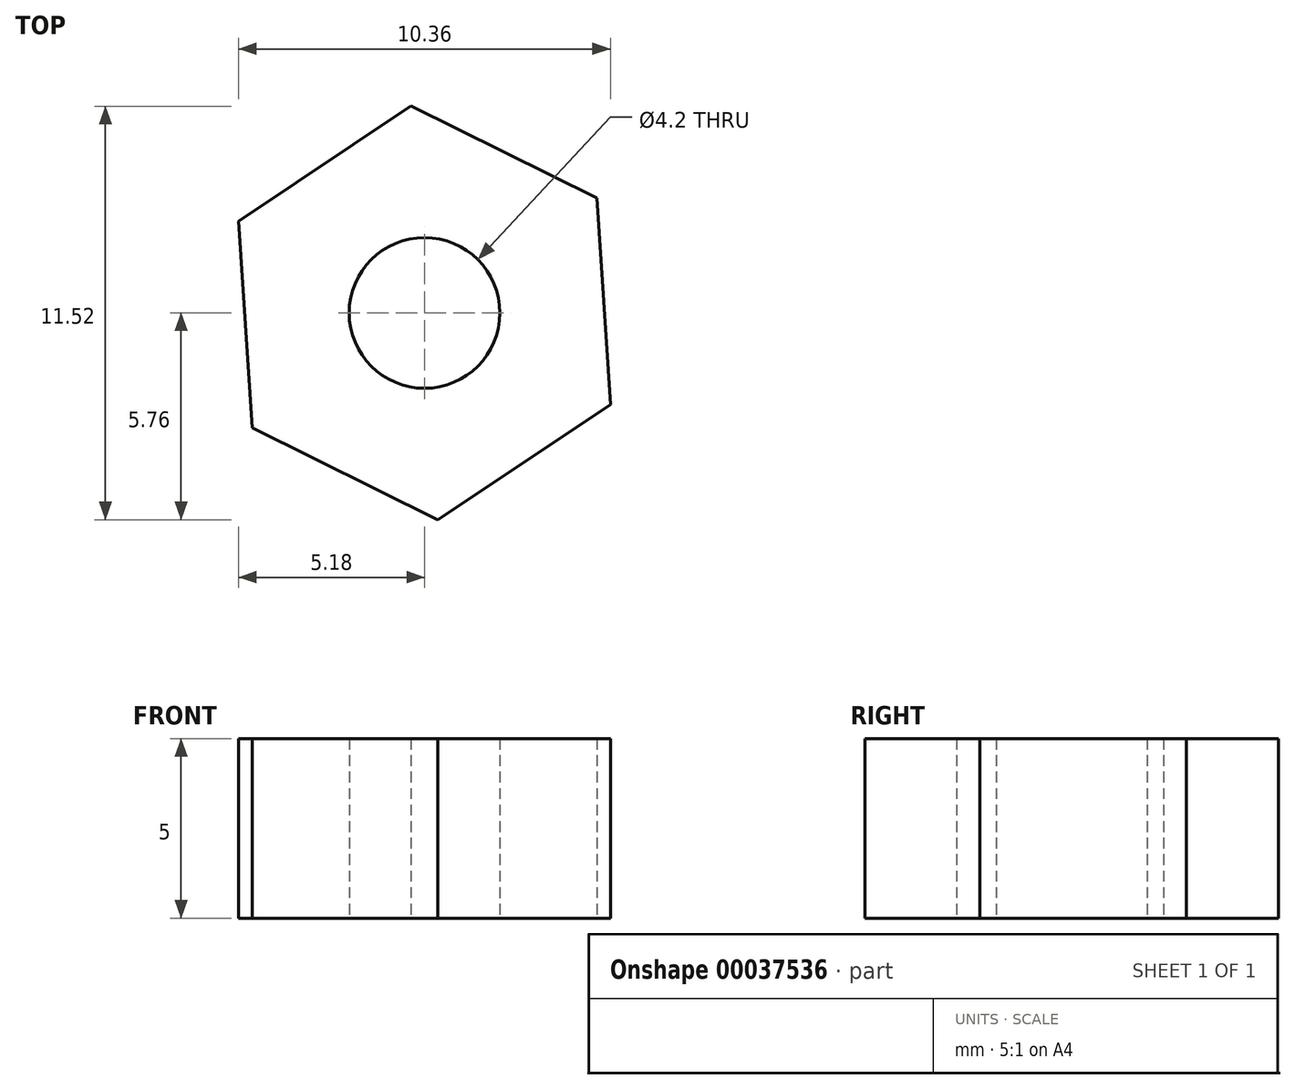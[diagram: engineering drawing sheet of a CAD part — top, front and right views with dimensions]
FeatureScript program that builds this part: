
annotation { "Feature Type Name" : "Feature", "Feature Type Description" : "" }
export const myFeature = defineFeature(function(context is Context, id is Id, definition is map)
    precondition{}
    {
        {
            var Q0;
            Q0=qCreatedBy(makeId("Top.planeOp"),FACE);
            var sketch = newSketch(context, id + "F0", { "sketchPlane" : qUnion([Q0])});
            skCircle(sketch, "E0", {"center": v(0, 0) * mm, "radius": 2.1 * mm});
            skCircle(sketch, "E1.cCircle", {"center": v(0, 0) * mm, "radius": 5 * mm, "construction": true});
            skLineSegment(sketch, "E1.0", {"start": v(-5.18, 2.56) * mm, "end": v(-0.37, 5.76) * mm});
            skLineSegment(sketch, "E1.1", {"start": v(-0.37, 5.76) * mm, "end": v(4.8, 3.2) * mm});
            skLineSegment(sketch, "E1.2", {"start": v(4.8, 3.2) * mm, "end": v(5.18, -2.56) * mm});
            skLineSegment(sketch, "E1.3", {"start": v(5.18, -2.56) * mm, "end": v(0.37, -5.76) * mm});
            skLineSegment(sketch, "E1.4", {"start": v(0.37, -5.76) * mm, "end": v(-4.8, -3.2) * mm});
            skLineSegment(sketch, "E1.5", {"start": v(-4.8, -3.2) * mm, "end": v(-5.18, 2.56) * mm});
            skPoint(sketch, "E1.0.midPoint", {"position": v(-2.77, 4.16) * mm});
            skSolve(sketch);
        }
        {
            var Q0;
            Q0=makeQuery(id+"F0.imprint","IMPRINT",FACE,{"disambiguationData":[TD([[makeQuery(id+"F0.imprint","IMPRINT",EDGE,{"derivedFrom":sQuery(id+"F0.wireOp",EDGE,"E0")}),-1.0]])]});
            extrude(context, id + "F1", {"entities" : qUnion([Q0]), "depth" : 5 * mm});
        }
    });
